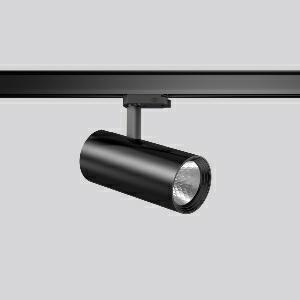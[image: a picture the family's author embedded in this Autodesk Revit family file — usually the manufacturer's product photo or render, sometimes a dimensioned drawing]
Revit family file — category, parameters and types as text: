
# Revit family: deecos_s_mini_742197_003_2_4799
name_source: partatom
category: Lighting Fixtures
units: mm (PartAtom-declared; Revit-internal decimal feet)

## family parameters
Cut with Voids When Loaded = No
Host = Face
Light Source = No
Part Type = Normal
Room Calculation Point = No
Round Connector Dimension = Use Diameter
Shared = No

## types (1)
- DEECOS S mini (1 x LED Modul 927, 2400 lm, 2700)
    Apparent Load = 20 VA
    Approval mark = CE
    CIE Flux Codes = 95 99 100 100 100
    Color Rendering = 92
    Color Temperature = 2700
    Default Elevation = 1800 mm
    Description = Series: DEECOS S mini
LED surface-mounted projector in modern design with no visible cooling ribs. Housing: die-cast aluminium, powder-coated. Rotation range: 356°. Swivel range: 90°. Black plastic ring and recessed LED to prevent glare from the side. Optical assembly with reflector made of MIRO-Silver with 98% total light reflection for outstanding efficiency - can be changed without tools. Best colour rendering index Ra>90. With multi adaptor for 3-circuit tracks 230 V. Suitable for Track on ceiling, Wall track. High quality converter without flickering and stroboscopic effect. The following accessories can be mounted without use of tools: interchangeable lenses, decorative glasses, honeycomb louvre, clear and frosted diffusers, white interchangeable plastic ring. 
Colour: deep black, matt (RAL 9005)
Diameter: 87 mm
Height: 214 mm
Lamp: LED
Socket: without socket
Colour temperature: 2700K
Colour rendering index (CRI): 92
System power: 20 W
Rated luminous flux: 2400 lm
Luminous efficiency: 120 lm/W
Control gear: Regulated power supply
Protection class: I
Type of protection: IP 20
    Height = 214 mm
    Lamp = 1 x LED Modul 927
    Lamp Light Flux = 2400 lm
    Lamp count = 1
    Length = 87 mm
    Lifetime = 50000 h
    Luminous efficacy = 120 lm/W
    Manufacturer = RZB
    ModVariant = No
    Model = 742197.003.2
    Mounting Place = Ceiling
    Mounting Type = Rail mounted
    Number of Poles = 1
    OnlyDefault = Yes
    Power Factor = 1
    Product Name = DEECOS S mini
    Product group = Track mounted projectors
    ProductGroupID = 301
    Protection Class = Protection class I
    Protection Degree = IP 20
    RLX_Detail_Level = 1
    RLX_Emergency_Light_Flux = 0 lm
    RLX_Emergency_Type = 0
    RLX_Emergency_Type_DB = No
    RlxData = <blob elided: 38925 chars, md5=64f6613d>
    Socket = socket
    Standby Power = 0 W
    System Light Flux = 2400 lm
    System Power = 20 W
    Type Comments = Product without accessories
    Type Image = 741926.003.jpg
    URL = http://relux.com
    VarID = ---
    Voltage = 230 V
    Voltage Range = 220-240 V
    Weight = 0.00 kg
    Width = 0 mm  [stored 0 ft]

note: [stored X ft] marks values corroborated as IEEE doubles in the binary element streams (Revit-internal decimal feet)

## geometry (parser evidence)
native form markers: Blend x4, Sweep x12
no freeform markers — native parametric forms only
